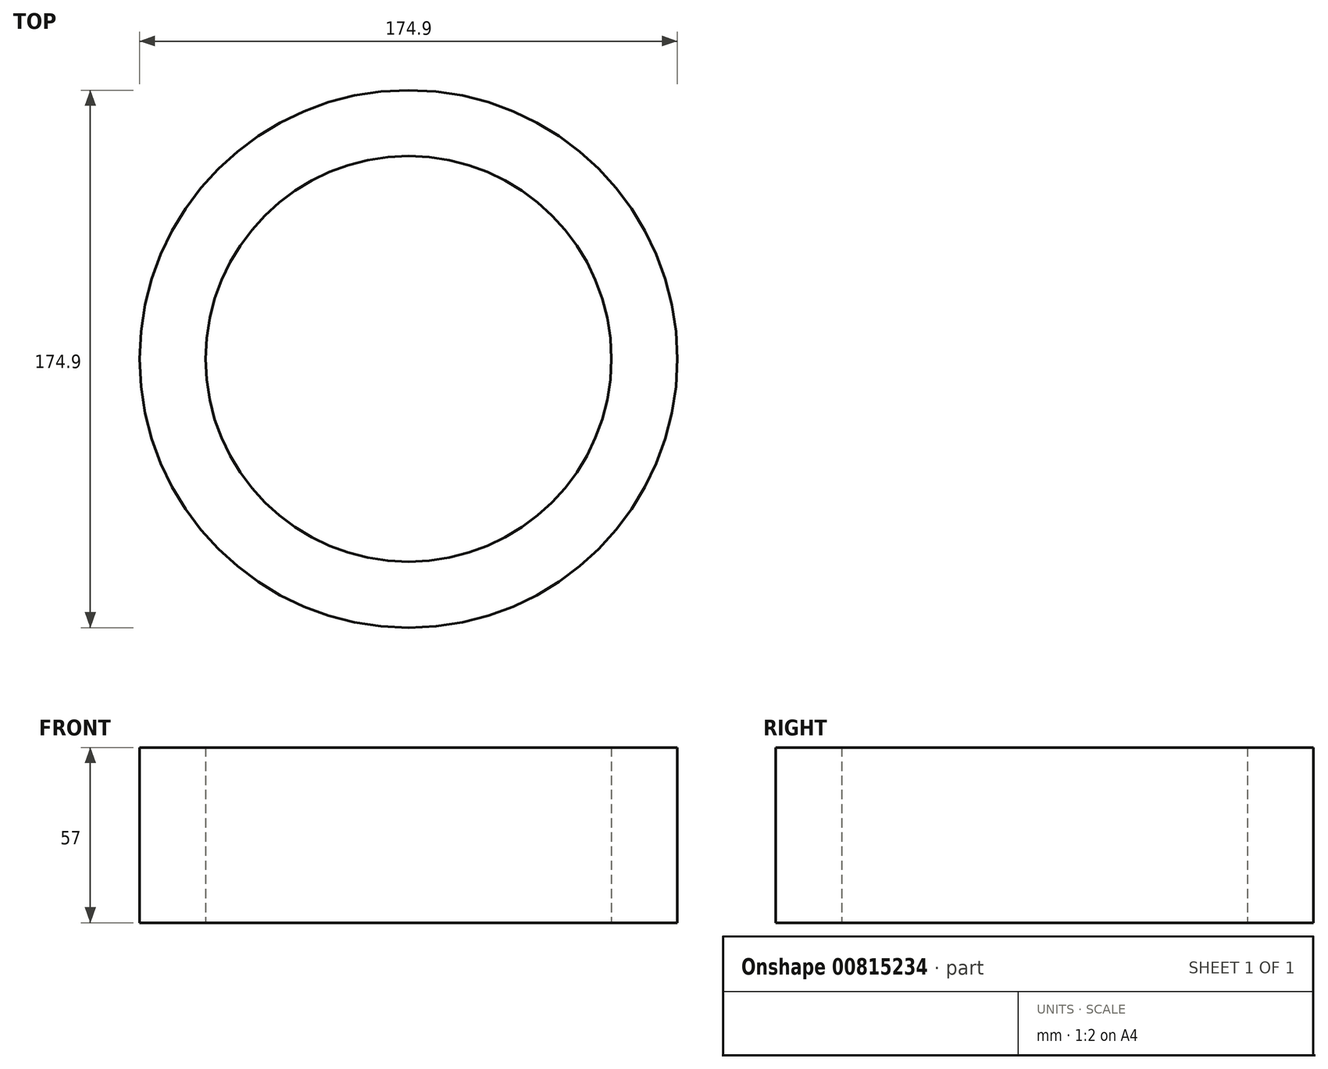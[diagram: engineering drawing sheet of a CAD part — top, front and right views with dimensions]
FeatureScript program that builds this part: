
annotation { "Feature Type Name" : "Feature", "Feature Type Description" : "" }
export const myFeature = defineFeature(function(context is Context, id is Id, definition is map)
    precondition{}
    {
        {
            var Q0;
            Q0=qCreatedBy(makeId("Top.planeOp"),FACE);
            var sketch = newSketch(context, id + "F0", { "sketchPlane" : qUnion([Q0])});
            skCircle(sketch, "E0", {"center": v(0, 0) * mm, "radius": 87.45 * mm});
            skCircle(sketch, "E1", {"center": v(0, 0) * mm, "radius": 66 * mm});
            skSolve(sketch);
        }
        {
            var Q0;
            Q0=qSketchRegion(id+"F0",true);
            extrude(context, id + "F1", {"entities" : qUnion([Q0]), "depth" : 32 * mm, "offsetDistance" : 25 * mm});
        }
        {
            var Q0;
            Q0=makeQuery(id+"F1.opExtrude","CAP_FACE",FACE,{"disambiguationData":[OSD([sQuery(id+"F0.wireOp",EDGE,"E0"),sQuery(id+"F0.wireOp",EDGE,"E1")])],"isStart":false});
            extrude(context, id + "F2", {"entities" : qUnion([Q0]), "operationType" : NewBodyOperationType.ADD, "depth" : 25 * mm, "offsetDistance" : 25 * mm});
        }
    });
